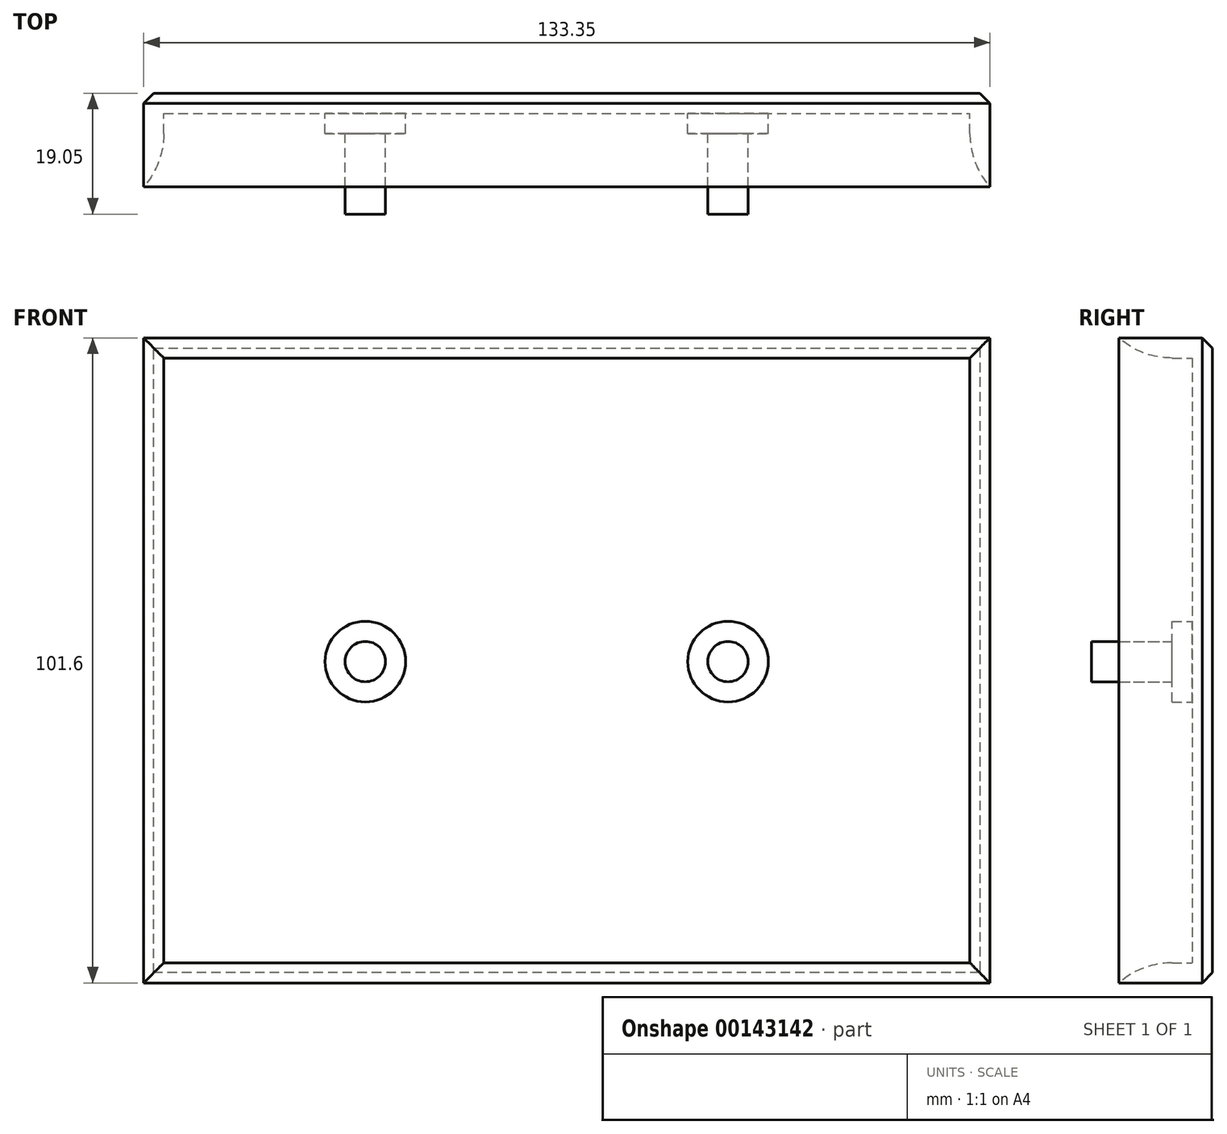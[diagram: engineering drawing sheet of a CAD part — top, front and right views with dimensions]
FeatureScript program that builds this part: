
annotation { "Feature Type Name" : "Feature", "Feature Type Description" : "" }
export const myFeature = defineFeature(function(context is Context, id is Id, definition is map)
    precondition{}
    {
        {
            var Q0;
            Q0=qCreatedBy(makeId("Front.planeOp"),FACE);
            var sketch = newSketch(context, id + "F0", { "sketchPlane" : qUnion([Q0])});
            skLineSegment(sketch, "E0.bottom", {"start": v(-100.94, 50.99) * mm, "end": v(32.4, 50.99) * mm});
            skLineSegment(sketch, "E0.top", {"start": v(-100.94, -50.61) * mm, "end": v(32.4, -50.61) * mm});
            skLineSegment(sketch, "E0.left", {"start": v(-100.94, 50.99) * mm, "end": v(-100.94, -50.61) * mm});
            skLineSegment(sketch, "E0.right", {"start": v(32.4, 50.99) * mm, "end": v(32.4, -50.61) * mm});
            skSolve(sketch);
        }
        {
            var Q0;
            Q0 = qSketchRegion(id + "F0", true);
            extrude(context, id + "F1", {"entities" : qUnion([Q0]), "depth" : 19.05 * mm});
        }
        {
            var Q0;
            Q0=makeQuery(id+"F1.opExtrude","CAP_FACE",FACE,{"disambiguationData":[OSD([sQuery(id+"F0.wireOp",EDGE,"E0.bottom"),sQuery(id+"F0.wireOp",EDGE,"E0.top"),sQuery(id+"F0.wireOp",EDGE,"E0.left"),sQuery(id+"F0.wireOp",EDGE,"E0.right")])],"isStart":false});
            shell(context, id + "F2", {"entities" : qUnion([Q0]), "thickness" : 3.17 * mm});
        }
        {
            var Q0;
            Q0=makeQuery(id+"F2.opShell","OFFSET_FACE",FACE,{"disambiguationData":[OSD([sQuery(id+"F0.wireOp",EDGE,"E0.bottom"),sQuery(id+"F0.wireOp",EDGE,"E0.top"),sQuery(id+"F0.wireOp",EDGE,"E0.left"),sQuery(id+"F0.wireOp",EDGE,"E0.right")])]});
            var sketch = newSketch(context, id + "F3", { "sketchPlane" : qUnion([Q0])});
            skCircle(sketch, "E1", {"center": v(-66.02, 0) * mm, "radius": 6.35 * mm});
            skCircle(sketch, "E2", {"center": v(-8.87, 0) * mm, "radius": 6.35 * mm});
            skSolve(sketch);
        }
        {
            var Q0;
            Q0 = qSketchRegion(id + "F3", true);
            extrude(context, id + "F4", {"entities" : qUnion([Q0]), "operationType" : NewBodyOperationType.ADD, "depth" : 3.17 * mm});
        }
        {
            var Q0;
            Q0=makeQuery(id+"F4.opExtrude","CAP_FACE",FACE,{"disambiguationData":[OSD([sQuery(id+"F3.wireOp",EDGE,"E1")])],"isStart":false});
            var sketch = newSketch(context, id + "F5", { "sketchPlane" : qUnion([Q0])});
            skCircle(sketch, "E3", {"center": v(-66.02, 0) * mm, "radius": 3.17 * mm});
            skSolve(sketch);
        }
        {
            var Q0;
            Q0 = qSketchRegion(id + "F5", true);
            extrude(context, id + "F6", {"entities" : qUnion([Q0]), "operationType" : NewBodyOperationType.ADD, "depth" : 12.7 * mm});
        }
        {
            var Q0;
            Q0=makeQuery(id+"F4.opExtrude","CAP_FACE",FACE,{"disambiguationData":[OSD([sQuery(id+"F3.wireOp",EDGE,"E2")])],"isStart":false});
            var sketch = newSketch(context, id + "F7", { "sketchPlane" : qUnion([Q0])});
            skCircle(sketch, "E4", {"center": v(-8.87, 0) * mm, "radius": 3.17 * mm});
            skSolve(sketch);
        }
        {
            var Q0;
            Q0 = qSketchRegion(id + "F7", true);
            extrude(context, id + "F8", {"entities" : qUnion([Q0]), "operationType" : NewBodyOperationType.ADD, "depth" : 12.7 * mm});
        }
        {
            var Q0;
            {var subQ0=sQuery(id+"F0.wireOp",EDGE,"E0.left");Q0=makeQuery(id+"F2.opShell","OFFSET_EDGE",EDGE,{"disambiguationData":[OSD([subQ0]),TDD([makeQuery(id+"F1.opExtrude","CAP_EDGE",EDGE,{"disambiguationData":[OSD([subQ0])],"isStart":false})])]});}
            var Q1;
            {var subQ0=sQuery(id+"F0.wireOp",EDGE,"E0.top");Q1=makeQuery(id+"F2.opShell","OFFSET_EDGE",EDGE,{"disambiguationData":[OSD([subQ0]),TDD([makeQuery(id+"F1.opExtrude","CAP_EDGE",EDGE,{"disambiguationData":[OSD([subQ0])],"isStart":false})])]});}
            var Q2;
            {var subQ0=sQuery(id+"F0.wireOp",EDGE,"E0.right");Q2=makeQuery(id+"F2.opShell","OFFSET_EDGE",EDGE,{"disambiguationData":[OSD([subQ0]),TDD([makeQuery(id+"F1.opExtrude","CAP_EDGE",EDGE,{"disambiguationData":[OSD([subQ0])],"isStart":false})])]});}
            var Q3;
            {var subQ0=sQuery(id+"F0.wireOp",EDGE,"E0.bottom");Q3=makeQuery(id+"F2.opShell","OFFSET_EDGE",EDGE,{"disambiguationData":[OSD([subQ0]),TDD([makeQuery(id+"F1.opExtrude","CAP_EDGE",EDGE,{"disambiguationData":[OSD([subQ0])],"isStart":false})])]});}
            fillet(context, id + "F9", {"entities" : qUnion([Q0, Q1, Q2, Q3]), "radius" : 12.7 * mm, "tangentPropagation" : true, "allowEdgeOverflow" : false});
        }
        {
            var Q0;
            Q0=makeQuery(id+"F1.opExtrude","CAP_EDGE",EDGE,{"disambiguationData":[OSD([sQuery(id+"F0.wireOp",EDGE,"E0.bottom")])],"isStart":true});
            var Q1;
            Q1=makeQuery(id+"F1.opExtrude","CAP_EDGE",EDGE,{"disambiguationData":[OSD([sQuery(id+"F0.wireOp",EDGE,"E0.left")])],"isStart":true});
            var Q2;
            Q2=makeQuery(id+"F1.opExtrude","CAP_EDGE",EDGE,{"disambiguationData":[OSD([sQuery(id+"F0.wireOp",EDGE,"E0.top")])],"isStart":true});
            var Q3;
            Q3=makeQuery(id+"F1.opExtrude","CAP_EDGE",EDGE,{"disambiguationData":[OSD([sQuery(id+"F0.wireOp",EDGE,"E0.right")])],"isStart":true});
            chamfer(context, id + "F10", {"entities" : qUnion([Q0, Q1, Q2, Q3]), "width" : 1.6 * mm, "tangentPropagation" : true});
        }
    });
